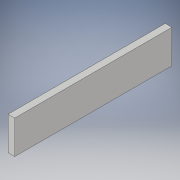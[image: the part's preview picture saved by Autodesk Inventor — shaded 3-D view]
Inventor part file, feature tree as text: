
AUTODESK INVENTOR PART (.ipt)
format: ipt  version: 2018 (Build 220112000, 112)  size: 93,184 bytes
history: native  units: in
note: dims shown in document units (in); Inventor stores cm internally (conversion verified against a paired STEP export)
features: extrude x1, sketch x1
ambient origin geometry x8: Origin, YZ Plane, XZ Plane, XY Plane, X Axis, Y Axis, Z Axis, Center Point
bodies: Solid1 (feature_tree)
feature tree (2):
  extrude  "Extrusion1"  Depth=6.4961in
  sketch  "Sketch1"  dims[d0=1.378in d1=6.4961in d2=0.2756in d3=0.0in]
